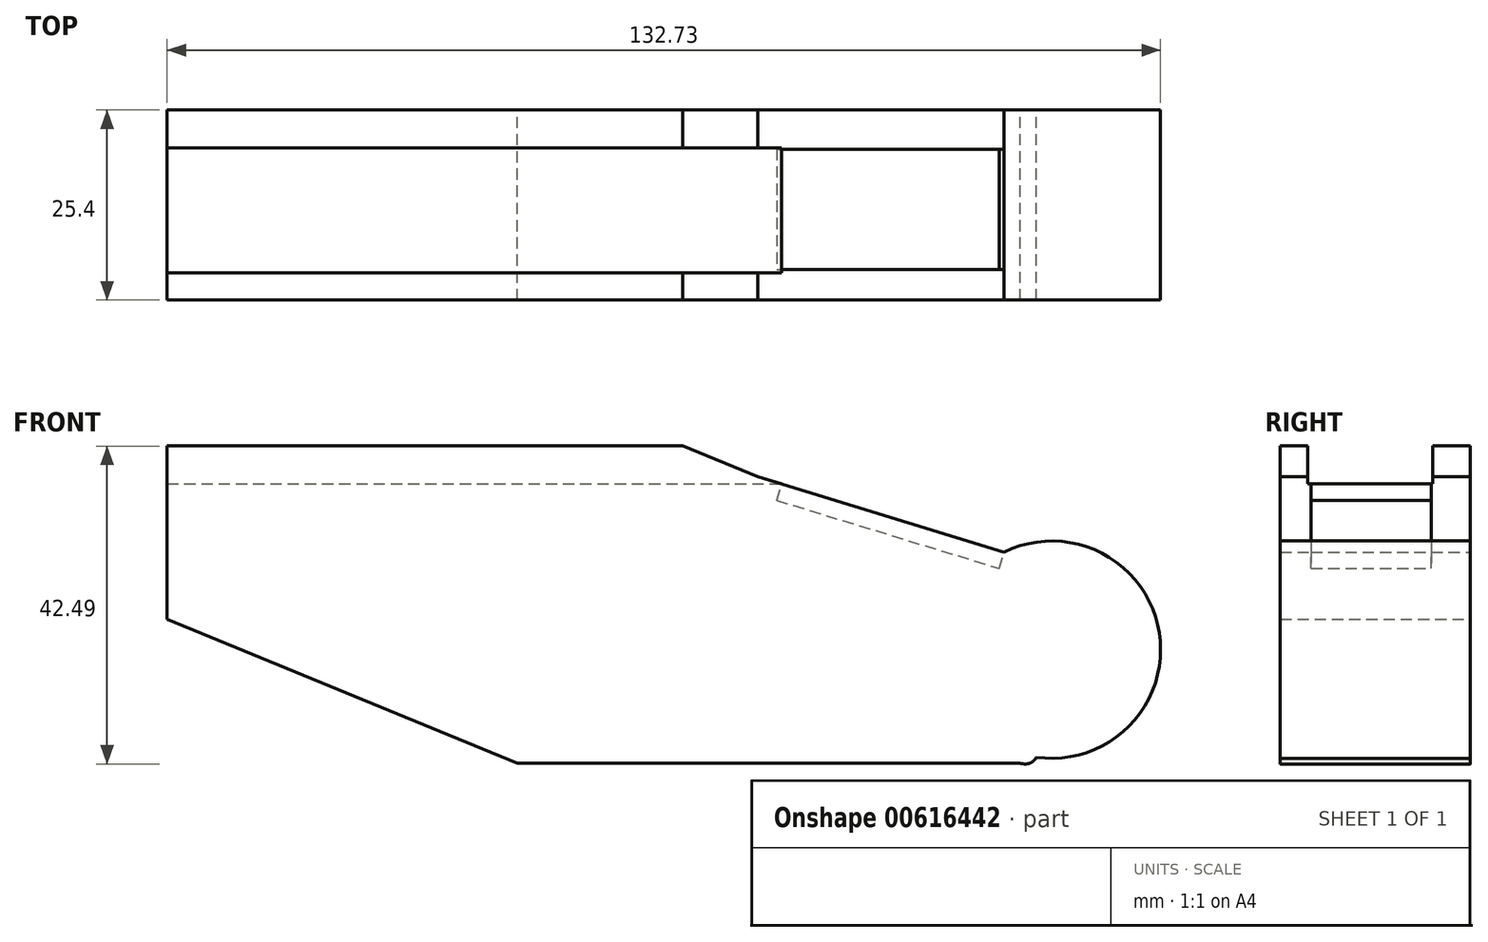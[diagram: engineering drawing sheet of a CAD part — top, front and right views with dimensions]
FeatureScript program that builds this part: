
annotation { "Feature Type Name" : "Feature", "Feature Type Description" : "" }
export const myFeature = defineFeature(function(context is Context, id is Id, definition is map)
    precondition{}
    {
        {
            var Q0;
            Q0=qCreatedBy(makeId("Front.planeOp"),FACE);
            var sketch = newSketch(context, id + "F0", { "sketchPlane" : qUnion([Q0])});
            skLineSegment(sketch, "E0.bottom", {"start": v(-51.74, 27.22) * mm, "end": v(17.14, 27.22) * mm});
            skLineSegment(sketch, "E0.left", {"start": v(-51.74, 27.22) * mm, "end": v(-51.74, 4.06) * mm});
            skLineSegment(sketch, "E1", {"start": v(58.35, -15.19) * mm, "end": v(-4.97, -15.19) * mm});
            skLineSegment(sketch, "E2", {"start": v(17.14, 27.22) * mm, "end": v(27.17, 23.12) * mm});
            skPoint(sketch, "E3.orphan", {"position": v(63.46, -15.19) * mm});
            skLineSegment(sketch, "E4", {"start": v(63.46, -15.19) * mm, "end": v(58.35, -15.19) * mm});
            skArc(sketch, "E5", {"start": v(64.4, -14.38) * mm, "mid": v(80.82, 2.25) * mm, "end": v(60.1, 13.05) * mm});
            skLineSegment(sketch, "E6", {"start": v(27.17, 23.12) * mm, "end": v(60.1, 13.05) * mm});
            skFitSpline(sketch, "E7", {"points": [v(60.1, 13.05) * mm, v(63.46, -15.19) * mm, v(53.66, -6.84) * mm, v(54.14, 7.67) * mm], "startDerivative": vector(29.74, -99.06) * mm, "endDerivative": vector(20.24, 56.06) * mm});
            skLineSegment(sketch, "E8", {"start": v(-51.74, 4.06) * mm, "end": v(-4.97, -15.19) * mm});
            skSolve(sketch);
        }
        {
            var Q0;
            Q0 = qSketchRegion(id + "F0", true);
            extrude(context, id + "F1", {"entities" : qUnion([Q0]), "depth" : 25.4 * mm, "offsetDistance" : 25.4 * mm});
        }
        {
            var Q0;
            Q0=makeQuery(id+"F1.opExtrude","SWEPT_FACE",FACE,{"disambiguationData":[OSD([sQuery(id+"F0.wireOp",EDGE,"E0.bottom")])]});
            var sketch = newSketch(context, id + "F2", { "sketchPlane" : qUnion([Q0])});
            skLineSegment(sketch, "E9.bottom", {"start": v(-59.24, -5.03) * mm, "end": v(83.29, -5.03) * mm});
            skLineSegment(sketch, "E9.top", {"start": v(-59.24, -21.76) * mm, "end": v(83.29, -21.76) * mm});
            skLineSegment(sketch, "E9.left", {"start": v(-59.24, -5.03) * mm, "end": v(-59.24, -21.76) * mm});
            skLineSegment(sketch, "E9.right", {"start": v(83.29, -5.03) * mm, "end": v(83.29, -21.76) * mm});
            skSolve(sketch);
        }
        {
            var Q0;
            Q0 = qSketchRegion(id + "F2", true);
            extrude(context, id + "F3", {"entities" : qUnion([Q0]), "operationType" : NewBodyOperationType.REMOVE, "oppositeDirection" : true, "depth" : 5.08 * mm, "offsetDistance" : 25.4 * mm});
        }
        {
            var Q0;
            Q0=makeQuery(id+"F1.opExtrude","SWEPT_FACE",FACE,{"disambiguationData":[OSD([sQuery(id+"F0.wireOp",EDGE,"E6")])]});
            var sketch = newSketch(context, id + "F4", { "sketchPlane" : qUnion([Q0])});
            skLineSegment(sketch, "E10.bottom", {"start": v(22.57, -21.29) * mm, "end": v(53.66, -21.29) * mm});
            skLineSegment(sketch, "E10.top", {"start": v(22.57, -5.22) * mm, "end": v(53.66, -5.22) * mm});
            skLineSegment(sketch, "E10.left", {"start": v(22.57, -21.29) * mm, "end": v(22.57, -5.22) * mm});
            skLineSegment(sketch, "E10.right", {"start": v(53.66, -21.29) * mm, "end": v(53.66, -5.22) * mm});
            skSolve(sketch);
        }
        {
            var Q0;
            Q0 = qSketchRegion(id + "F4", true);
            extrude(context, id + "F5", {"entities" : qUnion([Q0]), "operationType" : NewBodyOperationType.REMOVE, "oppositeDirection" : true, "depth" : 2.3 * mm, "offsetDistance" : 25.4 * mm});
        }
    });
